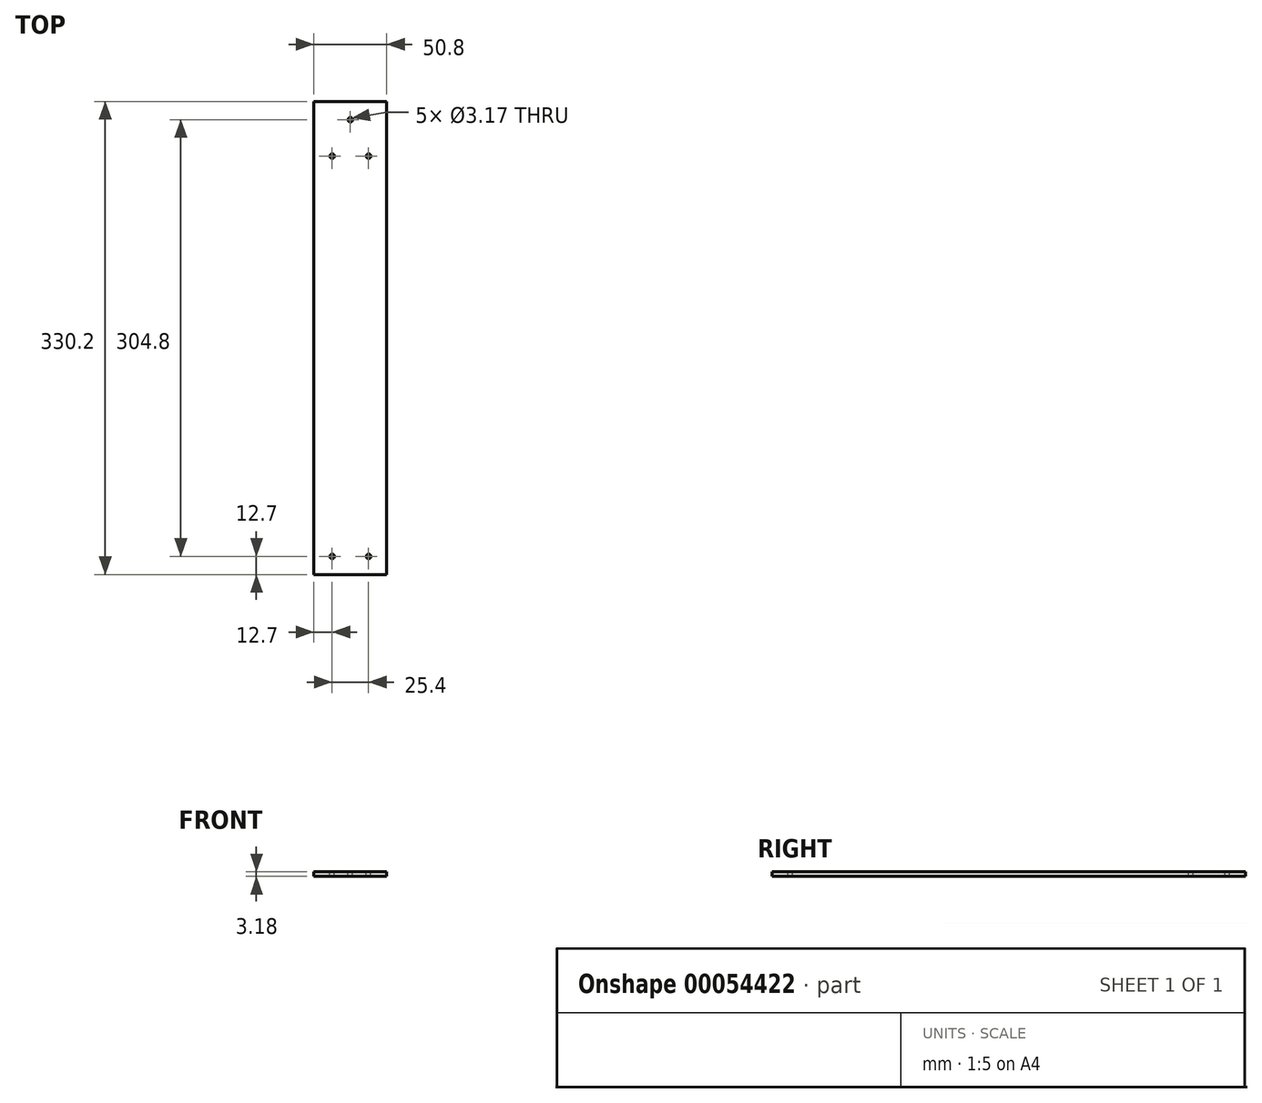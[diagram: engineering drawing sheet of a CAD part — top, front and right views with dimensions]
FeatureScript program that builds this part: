
annotation { "Feature Type Name" : "Feature", "Feature Type Description" : "" }
export const myFeature = defineFeature(function(context is Context, id is Id, definition is map)
    precondition{}
    {
        {
            var Q0;
            Q0=qCreatedBy(makeId("Top.planeOp"),FACE);
            var sketch = newSketch(context, id + "F0", { "sketchPlane" : qUnion([Q0])});
            skLineSegment(sketch, "E0.bottom", {"start": v(0, 0) * mm, "end": v(50.8, 0) * mm});
            skLineSegment(sketch, "E0.top", {"start": v(0, 330.2) * mm, "end": v(50.8, 330.2) * mm});
            skLineSegment(sketch, "E0.left", {"start": v(0, 0) * mm, "end": v(0, 330.2) * mm});
            skLineSegment(sketch, "E0.right", {"start": v(50.8, 0) * mm, "end": v(50.8, 330.2) * mm});
            skSolve(sketch);
        }
        {
            var Q0;
            Q0=makeQuery(id+"F0.imprint","IMPRINT",FACE,{"disambiguationData":[TD([[makeQuery(id+"F0.imprint","IMPRINT",EDGE,{"derivedFrom":sQuery(id+"F0.wireOp",EDGE,"E0.bottom")}),1.0]])]});
            extrude(context, id + "F1", {"entities" : qUnion([Q0]), "depth" : 3.17 * mm});
        }
        {
            var Q0;
            Q0=makeQuery(id+"F1.opExtrude","CAP_FACE",FACE,{"disambiguationData":[OSD([sQuery(id+"F0.wireOp",EDGE,"E0.bottom"),sQuery(id+"F0.wireOp",EDGE,"E0.top"),sQuery(id+"F0.wireOp",EDGE,"E0.left"),sQuery(id+"F0.wireOp",EDGE,"E0.right")])],"isStart":false});
            var sketch = newSketch(context, id + "F2", { "sketchPlane" : qUnion([Q0])});
            skLineSegment(sketch, "E1", {"start": v(25.4, 330.2) * mm, "end": v(25.4, 0) * mm});
            skPoint(sketch, "E2", {"position": v(12.7, 12.7) * mm});
            skPoint(sketch, "E3", {"position": v(12.7, 292.1) * mm});
            skPoint(sketch, "E4.MirrorP", {"position": v(38.1, 12.7) * mm});
            skPoint(sketch, "E5.MirrorP", {"position": v(38.1, 292.1) * mm});
            skPoint(sketch, "E6", {"position": v(25.4, 317.5) * mm});
            skSolve(sketch);
        }
        {
            var Q0;
            Q0=sQuery(id+"F2.wireOp",VERTEX,"E3");
            var Q1;
            Q1=sQuery(id+"F2.wireOp",VERTEX,"E6");
            var Q2;
            Q2=sQuery(id+"F2.wireOp",VERTEX,"E5.MirrorP");
            var Q3;
            Q3=sQuery(id+"F2.wireOp",VERTEX,"E2");
            var Q4;
            Q4=sQuery(id+"F2.wireOp",VERTEX,"E4.MirrorP");
            var Q5;
            Q5=makeQuery(id+"F1.opExtrude","SWEPT_BODY",BODY,{"disambiguationData":[OSD([sQuery(id+"F0.wireOp",EDGE,"E0.bottom"),sQuery(id+"F0.wireOp",EDGE,"E0.top"),sQuery(id+"F0.wireOp",EDGE,"E0.left"),sQuery(id+"F0.wireOp",EDGE,"E0.right")])]});
            hole(context, id + "F3", {"style" : HoleStyle.SIMPLE, "holeDiameter" : 3.17 * mm, "endStyle" : HoleEndStyle.THROUGH, "locations" : qUnion([Q0, Q1, Q2, Q3, Q4]), "scope" : qUnion([Q5])});
        }
    });
